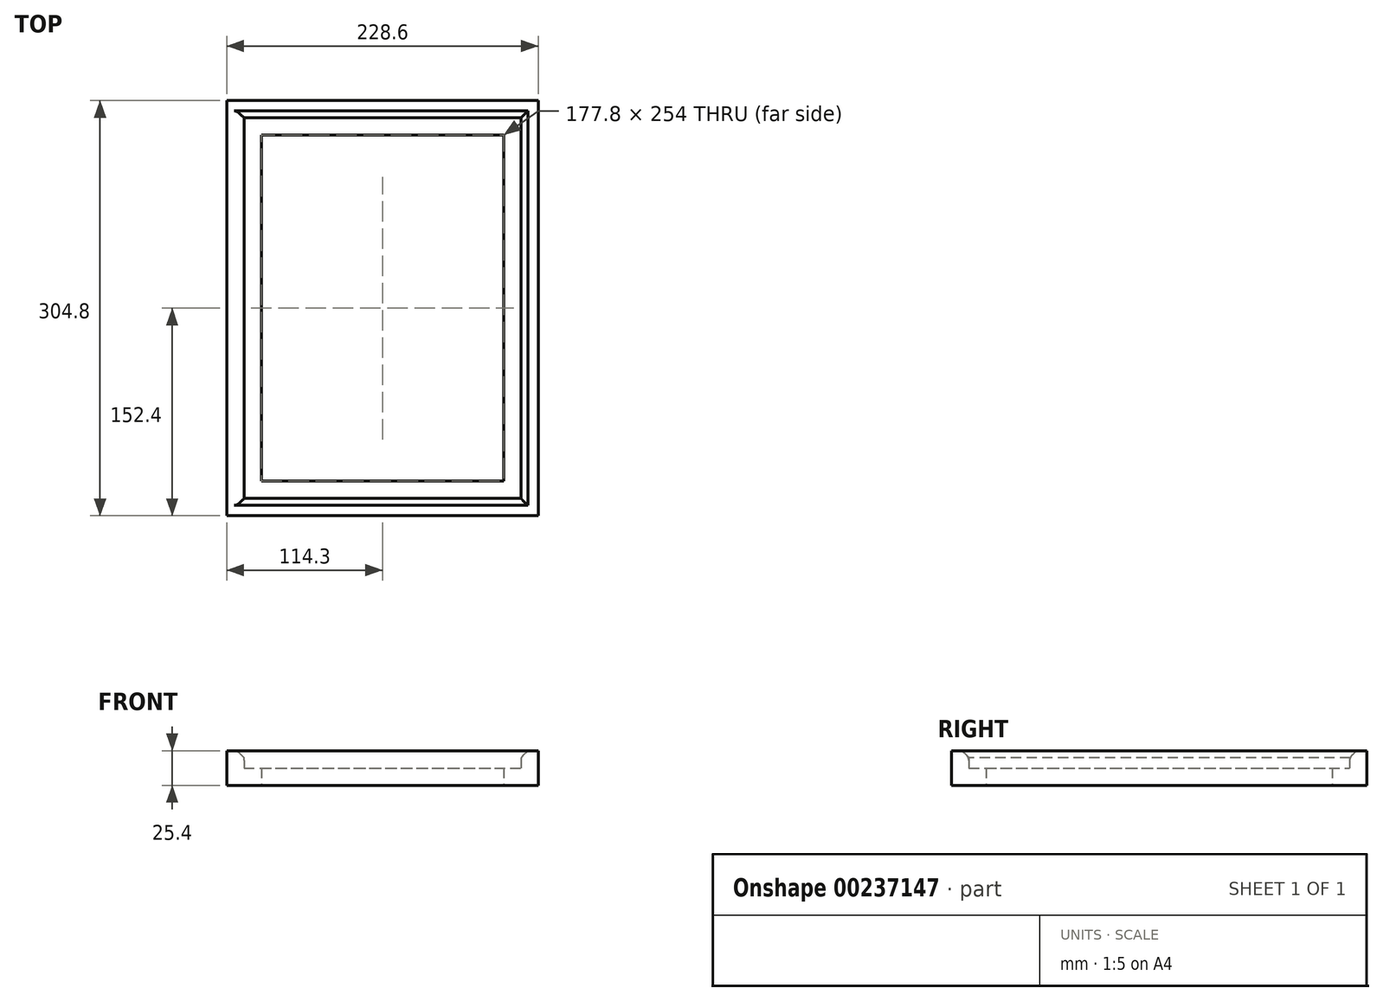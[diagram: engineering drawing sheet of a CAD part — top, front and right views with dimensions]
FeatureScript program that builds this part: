
annotation { "Feature Type Name" : "Feature", "Feature Type Description" : "" }
export const myFeature = defineFeature(function(context is Context, id is Id, definition is map)
    precondition{}
    {
        {
            var Q0;
            Q0=qCreatedBy(makeId("Top.planeOp"),FACE);
            var sketch = newSketch(context, id + "F0", { "sketchPlane" : qUnion([Q0])});
            skLineSegment(sketch, "E0.bottom", {"start": v(0, 0) * mm, "end": v(228.6, 0) * mm});
            skLineSegment(sketch, "E0.top", {"start": v(0, 304.8) * mm, "end": v(228.6, 304.8) * mm});
            skLineSegment(sketch, "E0.left", {"start": v(0, 0) * mm, "end": v(0, 304.8) * mm});
            skLineSegment(sketch, "E0.right", {"start": v(228.6, 0) * mm, "end": v(228.6, 304.8) * mm});
            skLineSegment(sketch, "E1.0", {"start": v(25.4, 279.4) * mm, "end": v(203.2, 279.4) * mm});
            skLineSegment(sketch, "E1.1", {"start": v(25.4, 25.4) * mm, "end": v(25.4, 279.4) * mm});
            skLineSegment(sketch, "E1.2", {"start": v(25.4, 25.4) * mm, "end": v(203.2, 25.4) * mm});
            skLineSegment(sketch, "E1.3", {"start": v(203.2, 25.4) * mm, "end": v(203.2, 279.4) * mm});
            skLineSegment(sketch, "E2.0", {"start": v(12.7, 292.1) * mm, "end": v(215.9, 292.1) * mm});
            skLineSegment(sketch, "E2.1", {"start": v(12.7, 12.7) * mm, "end": v(12.7, 292.1) * mm});
            skLineSegment(sketch, "E2.2", {"start": v(12.7, 12.7) * mm, "end": v(215.9, 12.7) * mm});
            skLineSegment(sketch, "E2.3", {"start": v(215.9, 12.7) * mm, "end": v(215.9, 292.1) * mm});
            skSolve(sketch);
        }
        {
            var Q0;
            Q0=makeQuery(id+"F0.imprint","IMPRINT",FACE,{"disambiguationData":[TD([[makeQuery(id+"F0.imprint","IMPRINT",EDGE,{"derivedFrom":sQuery(id+"F0.wireOp",EDGE,"E0.bottom")}),1.0]])]});
            extrude(context, id + "F1", {"entities" : qUnion([Q0]), "depth" : 25.4 * mm});
        }
        {
            var Q0;
            Q0=makeQuery(id+"F0.imprint","IMPRINT",FACE,{"disambiguationData":[TD([[makeQuery(id+"F0.imprint","IMPRINT",EDGE,{"derivedFrom":sQuery(id+"F0.wireOp",EDGE,"E1.0")}),1.0]])]});
            extrude(context, id + "F2", {"entities" : qUnion([Q0]), "operationType" : NewBodyOperationType.ADD, "depth" : 12.7 * mm});
        }
        {
            var Q0;
            Q0=makeQuery(id+"F1.opExtrude","CAP_EDGE",EDGE,{"disambiguationData":[OSD([sQuery(id+"F0.wireOp",EDGE,"E2.0")])],"isStart":false});
            var Q1;
            Q1=makeQuery(id+"F1.opExtrude","CAP_EDGE",EDGE,{"disambiguationData":[OSD([sQuery(id+"F0.wireOp",EDGE,"E2.3")])],"isStart":false});
            var Q2;
            Q2=makeQuery(id+"F1.opExtrude","CAP_EDGE",EDGE,{"disambiguationData":[OSD([sQuery(id+"F0.wireOp",EDGE,"E2.1")])],"isStart":false});
            var Q3;
            Q3=makeQuery(id+"F1.opExtrude","CAP_EDGE",EDGE,{"disambiguationData":[OSD([sQuery(id+"F0.wireOp",EDGE,"E2.2")])],"isStart":false});
            chamfer(context, id + "F3", {"entities" : qUnion([Q0, Q1, Q2, Q3]), "width" : 5.08 * mm, "tangentPropagation" : true});
        }
        {
            var Q0;
            {var subQ0=sQuery(id+"F0.wireOp",EDGE,"E2.0");Q0=makeQuery(id+"F3.opChamfer","BLEND_EDGE",EDGE,{"blendedFrom":[makeQuery(id+"F1.opExtrude","CAP_EDGE",EDGE,{"disambiguationData":[OSD([subQ0])],"isStart":false}),makeQuery(id+"F1.opExtrude","SWEPT_FACE",FACE,{"disambiguationData":[OSD([subQ0])]})],"blendedInto":[makeQuery(id+"F1.opExtrude","SWEPT_FACE",FACE,{"disambiguationData":[OSD([subQ0])]})]});}
            var Q1;
            {var subQ0=sQuery(id+"F0.wireOp",EDGE,"E2.3");Q1=makeQuery(id+"F3.opChamfer","BLEND_EDGE",EDGE,{"blendedFrom":[makeQuery(id+"F1.opExtrude","CAP_EDGE",EDGE,{"disambiguationData":[OSD([subQ0])],"isStart":false}),makeQuery(id+"F1.opExtrude","SWEPT_FACE",FACE,{"disambiguationData":[OSD([subQ0])]})],"blendedInto":[makeQuery(id+"F1.opExtrude","SWEPT_FACE",FACE,{"disambiguationData":[OSD([subQ0])]})]});}
            var Q2;
            {var subQ0=sQuery(id+"F0.wireOp",EDGE,"E2.1");Q2=makeQuery(id+"F3.opChamfer","BLEND_EDGE",EDGE,{"blendedFrom":[makeQuery(id+"F1.opExtrude","CAP_EDGE",EDGE,{"disambiguationData":[OSD([subQ0])],"isStart":false}),makeQuery(id+"F1.opExtrude","CAP_FACE",FACE,{"disambiguationData":[OSD([sQuery(id+"F0.wireOp",EDGE,"E0.bottom"),sQuery(id+"F0.wireOp",EDGE,"E0.top"),sQuery(id+"F0.wireOp",EDGE,"E0.left"),sQuery(id+"F0.wireOp",EDGE,"E0.right"),sQuery(id+"F0.wireOp",EDGE,"E2.0"),subQ0,sQuery(id+"F0.wireOp",EDGE,"E2.2"),sQuery(id+"F0.wireOp",EDGE,"E2.3")])],"isStart":false})],"blendedInto":[makeQuery(id+"F1.opExtrude","CAP_FACE",FACE,{"disambiguationData":[OSD([sQuery(id+"F0.wireOp",EDGE,"E0.bottom"),sQuery(id+"F0.wireOp",EDGE,"E0.top"),sQuery(id+"F0.wireOp",EDGE,"E0.left"),sQuery(id+"F0.wireOp",EDGE,"E0.right"),sQuery(id+"F0.wireOp",EDGE,"E2.0"),subQ0,sQuery(id+"F0.wireOp",EDGE,"E2.2"),sQuery(id+"F0.wireOp",EDGE,"E2.3")])],"isStart":false})]});}
            var Q3;
            {var subQ0=sQuery(id+"F0.wireOp",EDGE,"E2.2");Q3=makeQuery(id+"F3.opChamfer","BLEND_EDGE",EDGE,{"blendedFrom":[makeQuery(id+"F1.opExtrude","CAP_EDGE",EDGE,{"disambiguationData":[OSD([subQ0])],"isStart":false}),makeQuery(id+"F1.opExtrude","SWEPT_FACE",FACE,{"disambiguationData":[OSD([subQ0])]})],"blendedInto":[makeQuery(id+"F1.opExtrude","SWEPT_FACE",FACE,{"disambiguationData":[OSD([subQ0])]})]});}
            fillet(context, id + "F4", {"entities" : qUnion([Q0, Q1, Q2, Q3]), "radius" : 5.08 * mm, "tangentPropagation" : true, "allowEdgeOverflow" : false});
        }
    });
